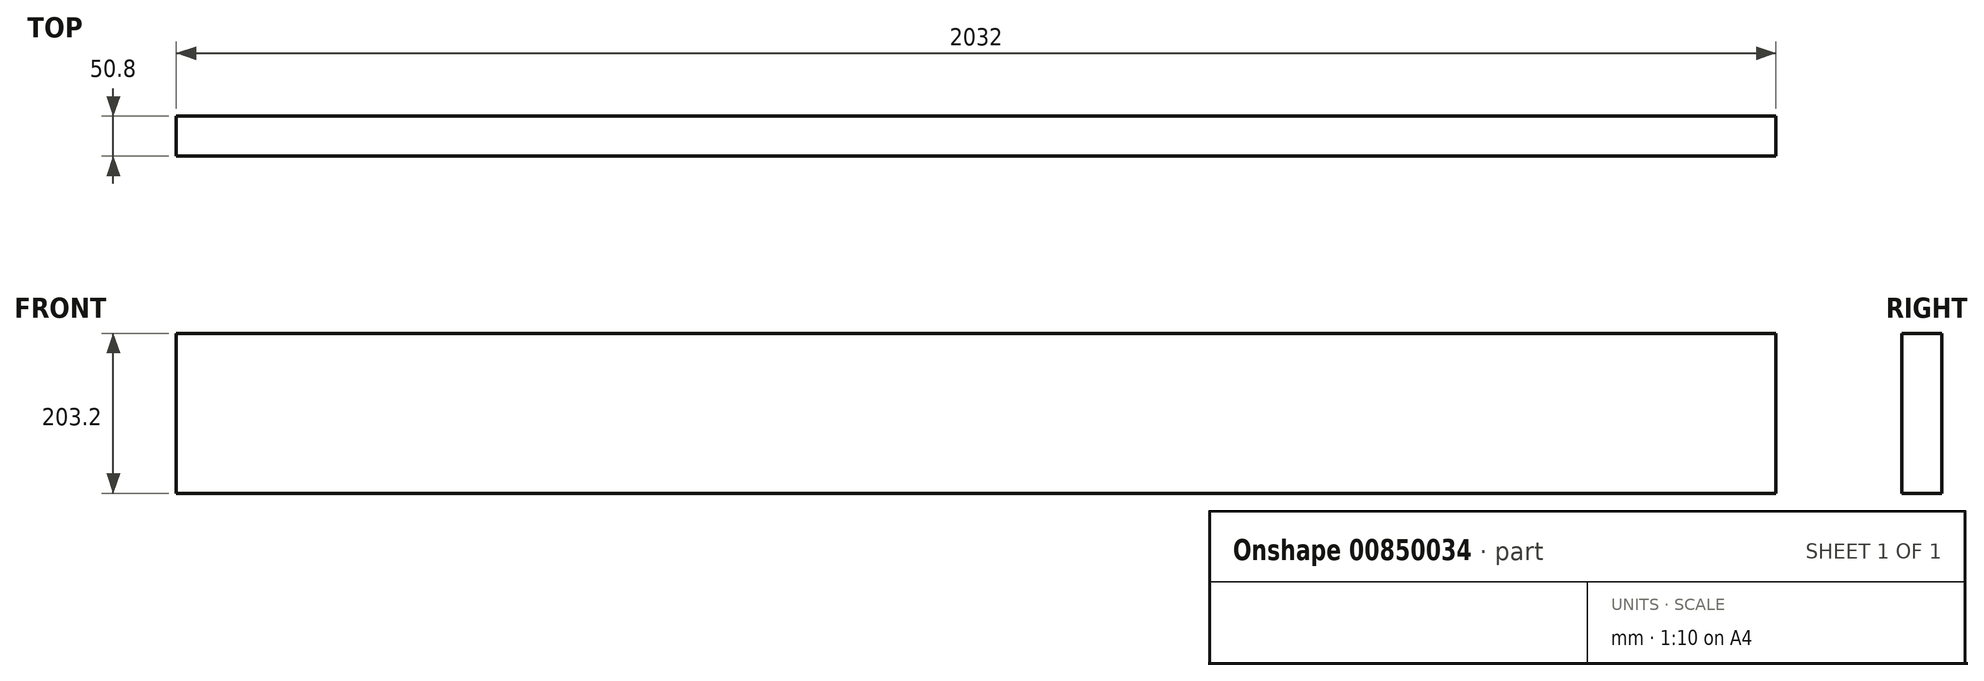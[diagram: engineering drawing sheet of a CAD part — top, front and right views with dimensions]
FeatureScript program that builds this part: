
annotation { "Feature Type Name" : "Feature", "Feature Type Description" : "" }
export const myFeature = defineFeature(function(context is Context, id is Id, definition is map)
    precondition{}
    {
        {
            var Q0;
            Q0=qCreatedBy(makeId("Top.planeOp"),FACE);
            var sketch = newSketch(context, id + "F0", { "sketchPlane" : qUnion([Q0])});
            skLineSegment(sketch, "E0.bottom", {"start": v(0, 0) * mm, "end": v(2032, 0) * mm});
            skLineSegment(sketch, "E0.top", {"start": v(0, -50.8) * mm, "end": v(2032, -50.8) * mm});
            skLineSegment(sketch, "E0.left", {"start": v(0, 0) * mm, "end": v(0, -50.8) * mm});
            skLineSegment(sketch, "E0.right", {"start": v(2032, 0) * mm, "end": v(2032, -50.8) * mm});
            skSolve(sketch);
        }
        {
            var Q0;
            Q0 = qSketchRegion(id + "F0", true);
            extrude(context, id + "F1", {"entities" : qUnion([Q0]), "depth" : 203.2 * mm, "offsetDistance" : 25.4 * mm});
        }
    });
